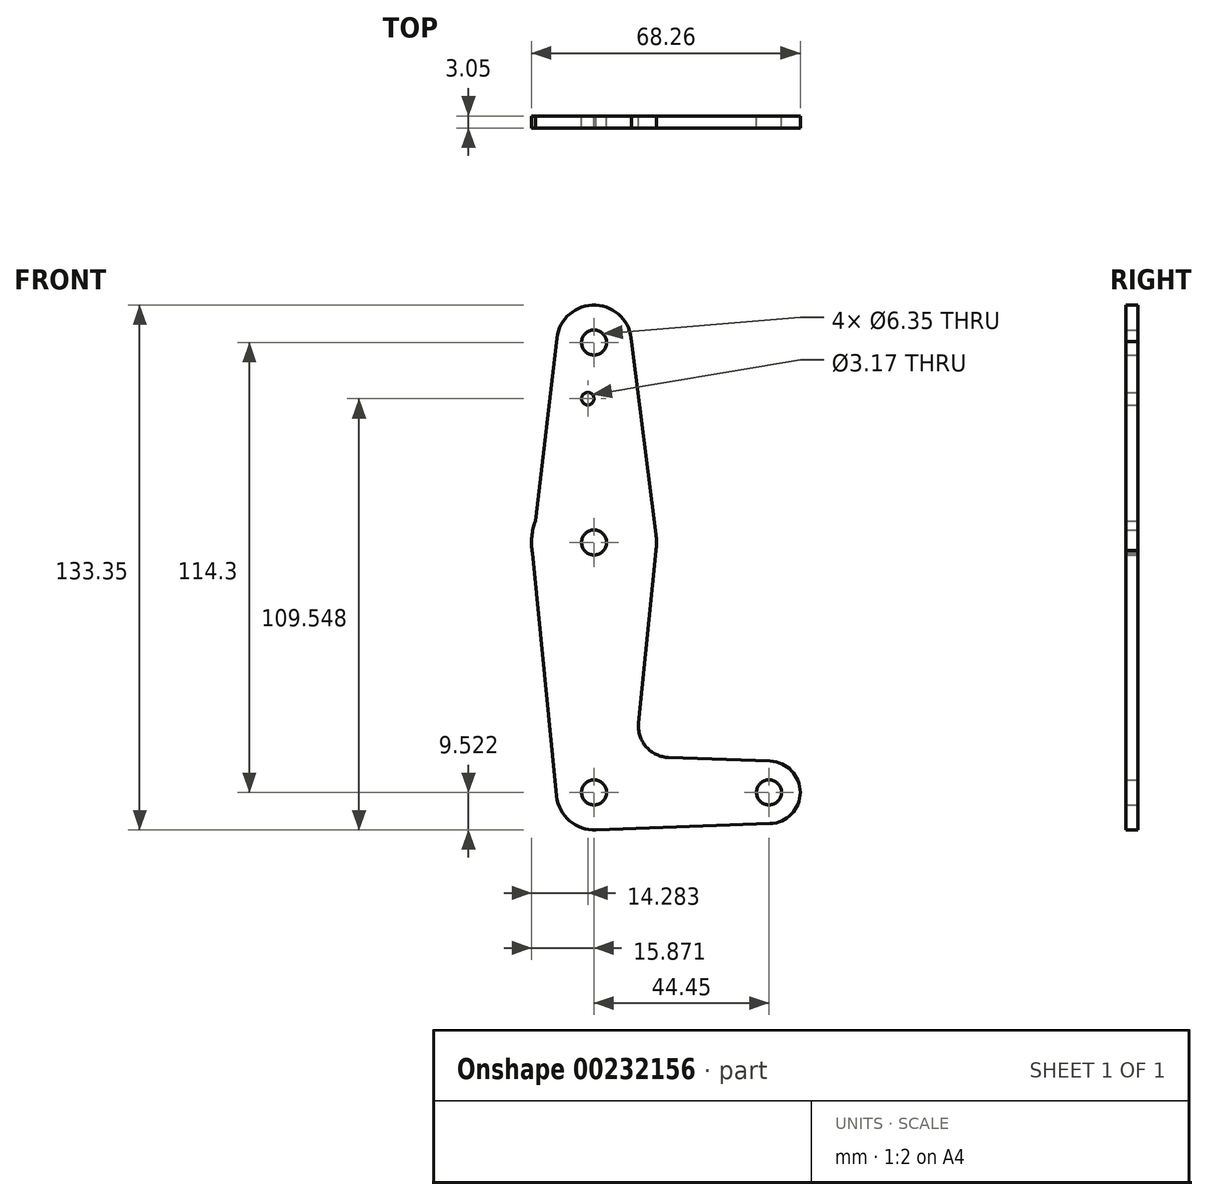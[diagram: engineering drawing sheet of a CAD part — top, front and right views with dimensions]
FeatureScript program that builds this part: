
annotation { "Feature Type Name" : "Feature", "Feature Type Description" : "" }
export const myFeature = defineFeature(function(context is Context, id is Id, definition is map)
    precondition{}
    {
        {
            var Q0;
            Q0=qCreatedBy(makeId("Front.planeOp"),FACE);
            var sketch = newSketch(context, id + "F0", { "sketchPlane" : qUnion([Q0])});
            skLineSegment(sketch, "E0", {"start": v(-39, 88.56) * mm, "end": v(-39, -25.74) * mm, "construction": true});
            skLineSegment(sketch, "E1", {"start": v(-39, -25.74) * mm, "end": v(5.44, -25.74) * mm, "construction": true});
            skCircle(sketch, "E2", {"center": v(-39, 88.56) * mm, "radius": 9.53 * mm});
            skCircle(sketch, "E3", {"center": v(-39, 37.76) * mm, "radius": 15.88 * mm});
            skCircle(sketch, "E4", {"center": v(-39, -25.74) * mm, "radius": 9.52 * mm});
            skCircle(sketch, "E5", {"center": v(5.44, -25.74) * mm, "radius": 7.94 * mm});
            skLineSegment(sketch, "E6", {"start": v(-54.88, 37.24) * mm, "end": v(-48.49, -26.68) * mm});
            skLineSegment(sketch, "E7", {"start": v(-29.73, 90.73) * mm, "end": v(-23.26, 39.76) * mm});
            skLineSegment(sketch, "E8", {"start": v(-23.18, 36.6) * mm, "end": v(-27.67, -8.15) * mm});
            skLineSegment(sketch, "E9", {"start": v(-20.04, -16.89) * mm, "end": v(5.72, -17.8) * mm});
            skLineSegment(sketch, "E10", {"start": v(-38.86, -35.26) * mm, "end": v(5.72, -33.67) * mm});
            skLineSegment(sketch, "E11", {"start": v(-48.47, 89.67) * mm, "end": v(-53.91, 43.23) * mm});
            skCircle(sketch, "E12", {"center": v(-40.6, 74.29) * mm, "radius": 1.59 * mm});
            skCircle(sketch, "E13", {"center": v(-39, 88.56) * mm, "radius": 3.18 * mm});
            skCircle(sketch, "E14", {"center": v(-39, 37.76) * mm, "radius": 3.18 * mm});
            skCircle(sketch, "E15", {"center": v(-39, -25.74) * mm, "radius": 3.18 * mm});
            skCircle(sketch, "E16", {"center": v(5.44, -25.74) * mm, "radius": 3.18 * mm});
            skArc(sketch, "E17.filletArc", {"start": v(-27.67, -8.15) * mm, "mid": v(-25.75, -14.17) * mm, "end": v(-20.04, -16.89) * mm});
            skSolve(sketch);
        }
        {
            var Q0;
            Q0 = qSketchRegion(id + "F0", true);
            extrude(context, id + "F1", {"entities" : qUnion([Q0]), "depth" : 3.05 * mm});
        }
    });
